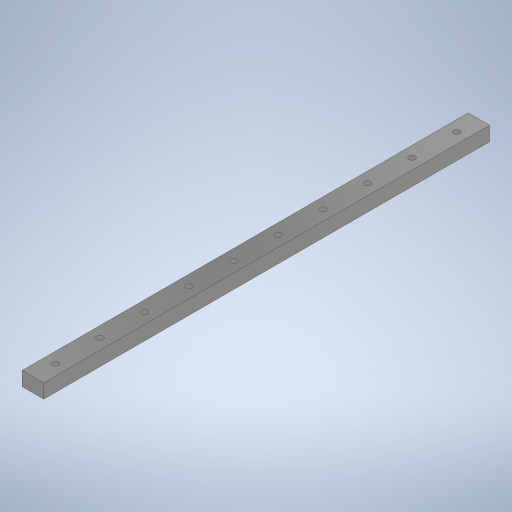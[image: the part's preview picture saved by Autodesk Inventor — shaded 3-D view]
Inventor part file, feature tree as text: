
AUTODESK INVENTOR PART (.ipt)
format: ipt  version: 2024 (Build 280153000, 153)  size: 260,608 bytes
history: native  units: mm
features: extrude x2, sketch x2
ambient origin geometry x8: Origin, YZ Plane, XZ Plane, XY Plane, X Axis, Y Axis, Z Axis, Center Point
bodies: Solid1 (feature_tree)
feature tree (4):
  extrude  "Extrusion1"  Depth=12.0mm
  extrude  "Extrusion2"  Depth=10.0mm
  sketch  "Sketch1"  dims[d0=250.0mm d1=12.0mm]
  sketch  "Sketch2"  dims[d2=8.0mm d3=0.0mm d4=3.5mm d5=6.0mm d6=12.5mm d7=100.0mm d9=25.0mm d10=10.0mm d12=10.0mm d14=0.0mm d15=0.0mm]
